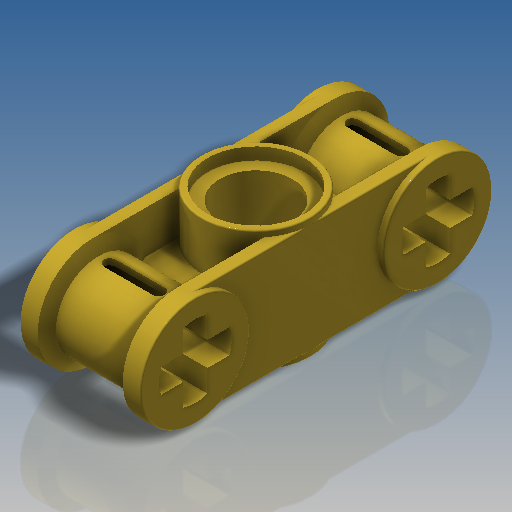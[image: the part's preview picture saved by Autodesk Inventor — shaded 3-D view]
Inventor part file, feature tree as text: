
AUTODESK INVENTOR PART (.ipt)
format: ipt  version: 2019.4 (Build 234330000, 330)  size: 481,792 bytes
history: native  units: in
note: dims shown in document units (in); Inventor stores cm internally (conversion verified against a paired STEP export)
features: extrude x6, sketch x4, mirror x2, plane x1, revolve x1, fillet x1
ambient origin geometry x8: Origin, YZ Plane, XZ Plane, XY Plane, X Axis, Y Axis, Z Axis, Center Point
bodies: Solid1 (feature_tree)
feature tree (15):
  sketch  "Sketch2"  dims[d0=0.2835in d1=0.189in]
  extrude  "Extrusion1"  Depth=0.189in
  plane  "Work Plane1"
  extrude  "Extrusion2"  Depth=0.315in TaperAngle=0.0deg
  extrude  "Extrusion4"  Depth=0.2835in
  extrude  "Extrusion3"  Depth=0.0039in TaperAngle=0.0deg
  mirror  "Mirror1"
  revolve  "Revolution1"  [1 undecoded]
  extrude  "Extrusion5"  Depth=0.0039in TaperAngle=0.0deg
  extrude  "Extrusion6"  Depth=0.0039in
  mirror  "Mirror2"
  fillet  "Fillet1"  Radius=0.0472in
  sketch  "Sketch3"  dims[d2=0.315in d3=0.315in d4=0.0in]
  sketch  "Sketch4"  dims[d5=0.0in d6=0.2835in]
  sketch  "Sketch5"  dims[d7=0.0315in d8=0.4724in d9=0.0in d10=0.252in d11=0.0315in d12=0.0in d13=0.2835in d14=0.0472in d15=0.315in d16=0.2205in d17=0.063in d18=0.0315in d19=0.1575in d20=90.0deg d21=0.063in d22=0.0in d23=0.063in d24=0.0in d25=0.189in d26=0.063in d27=0.063in d28=0.0in d29=0.0039in]
note: 1 required parameter value undecoded (feature->parameter linkage not recoverable at this tier; creation-order binding heuristic only, values carry confidence <= 0.55)
